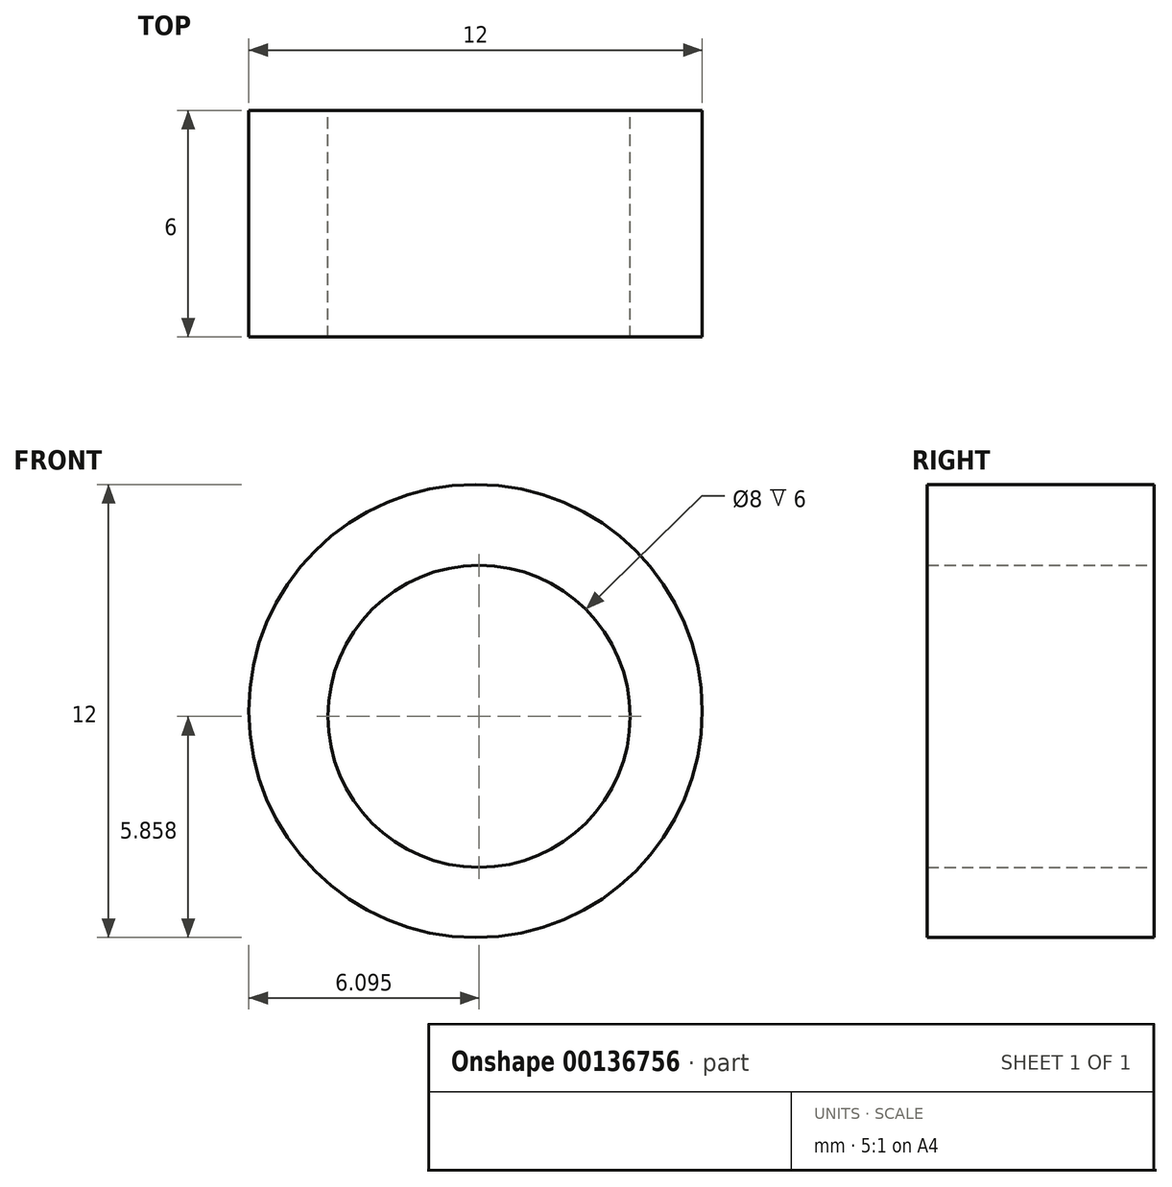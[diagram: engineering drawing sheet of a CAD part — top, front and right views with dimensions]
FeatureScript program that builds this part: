
annotation { "Feature Type Name" : "Feature", "Feature Type Description" : "" }
export const myFeature = defineFeature(function(context is Context, id is Id, definition is map)
    precondition{}
    {
        {
            var Q0;
            Q0=qCreatedBy(makeId("Front.planeOp"),FACE);
            var sketch = newSketch(context, id + "F0", { "sketchPlane" : qUnion([Q0])});
            skCircle(sketch, "E0", {"center": v(0, 0) * mm, "radius": 6 * mm});
            skCircle(sketch, "E1", {"center": v(0.1, -0.14) * mm, "radius": 4 * mm});
            skSolve(sketch);
        }
        {
            var Q0;
            Q0 = qSketchRegion(id + "F0", true);
            extrude(context, id + "F1", {"entities" : qUnion([Q0]), "depth" : 6 * mm});
        }
    });
